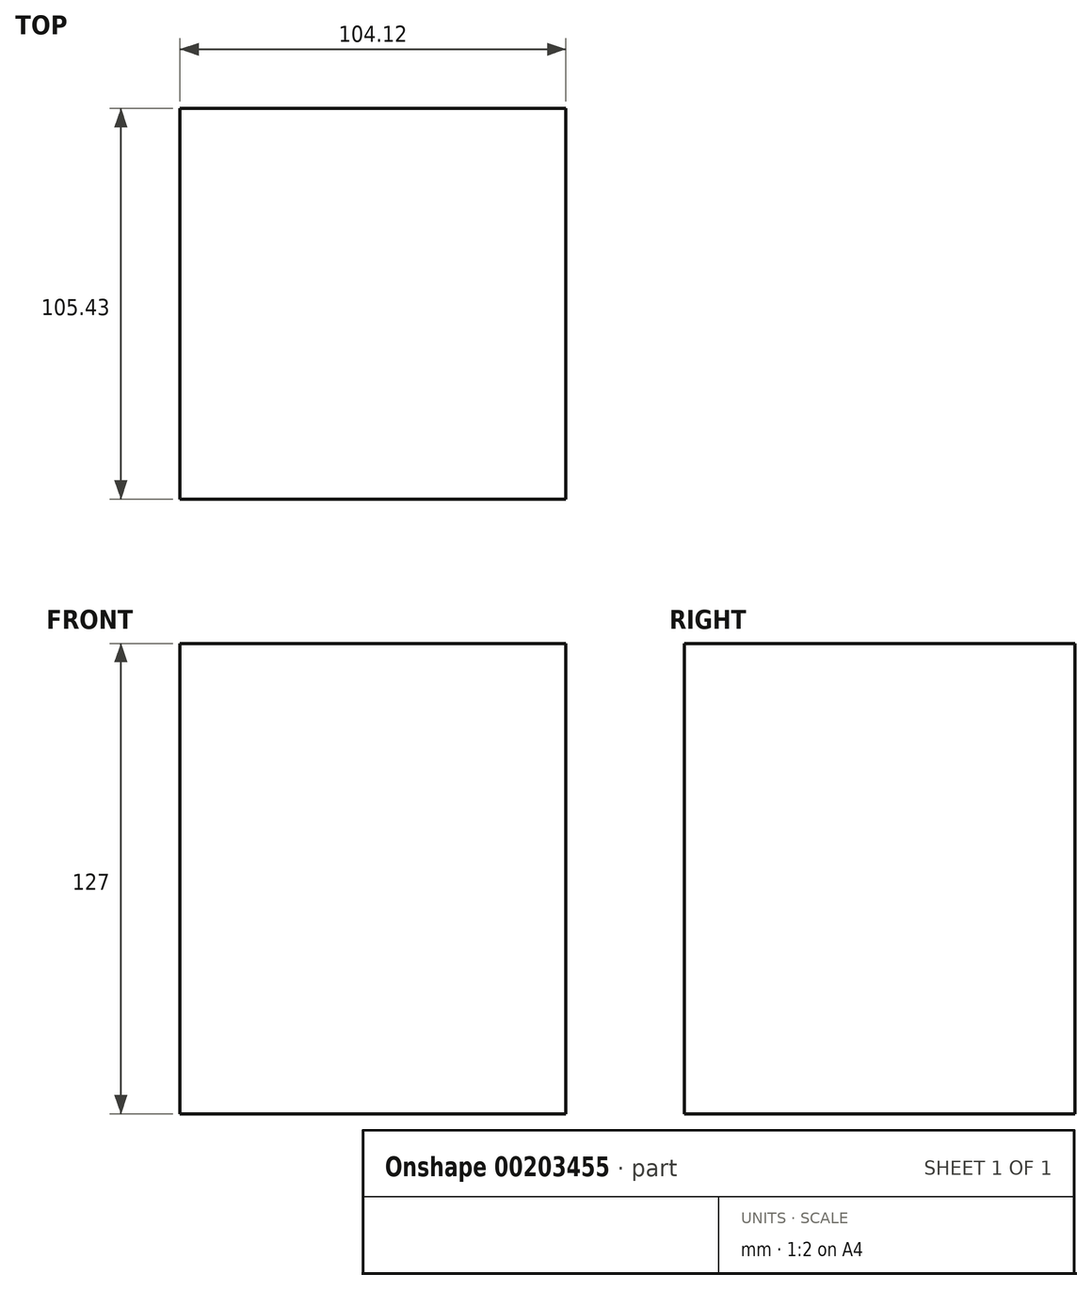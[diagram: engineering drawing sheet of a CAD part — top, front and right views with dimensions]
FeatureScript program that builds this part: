
annotation { "Feature Type Name" : "Feature", "Feature Type Description" : "" }
export const myFeature = defineFeature(function(context is Context, id is Id, definition is map)
    precondition{}
    {
        {
            var Q0;
            Q0=qCreatedBy(makeId("Top.planeOp"),FACE);
            var sketch = newSketch(context, id + "F0", { "sketchPlane" : qUnion([Q0])});
            skLineSegment(sketch, "E0.bottom", {"start": v(16.74, -37.11) * mm, "end": v(-87.38, -37.11) * mm});
            skLineSegment(sketch, "E0.top", {"start": v(16.74, 68.32) * mm, "end": v(-87.38, 68.32) * mm});
            skLineSegment(sketch, "E0.left", {"start": v(16.74, -37.11) * mm, "end": v(16.74, 68.32) * mm});
            skLineSegment(sketch, "E0.right", {"start": v(-87.38, -37.11) * mm, "end": v(-87.38, 68.32) * mm});
            skSolve(sketch);
        }
        {
            var Q0;
            Q0 = qSketchRegion(id + "F0", true);
            extrude(context, id + "F1", {"entities" : qUnion([Q0]), "depth" : 127 * mm});
        }
    });
